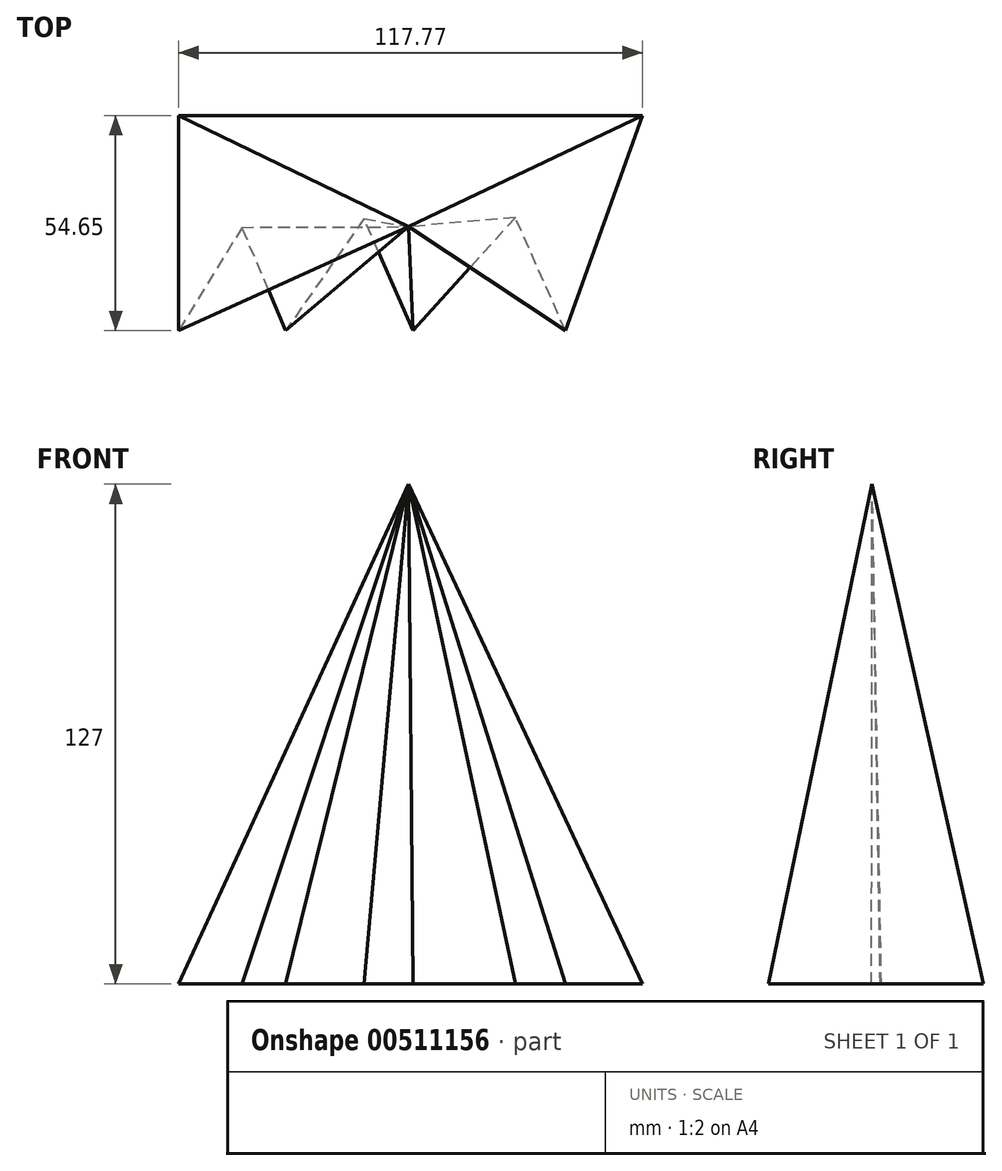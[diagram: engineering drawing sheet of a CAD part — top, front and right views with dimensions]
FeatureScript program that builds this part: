
annotation { "Feature Type Name" : "Feature", "Feature Type Description" : "" }
export const myFeature = defineFeature(function(context is Context, id is Id, definition is map)
    precondition{}
    {
        {
            var Q0;
            Q0=qCreatedBy(makeId("Top.planeOp"),FACE);
            var sketch = newSketch(context, id + "F0", { "sketchPlane" : qUnion([Q0])});
            skLineSegment(sketch, "E0", {"start": v(-59.46, 54.65) * mm, "end": v(58.3, 54.65) * mm});
            skLineSegment(sketch, "E1", {"start": v(58.3, 54.65) * mm, "end": v(38.77, 0) * mm});
            skLineSegment(sketch, "E2", {"start": v(38.77, 0) * mm, "end": v(26.04, 28.72) * mm});
            skLineSegment(sketch, "E3", {"start": v(26.04, 28.72) * mm, "end": v(0, 0) * mm});
            skLineSegment(sketch, "E4", {"start": v(0, 0) * mm, "end": v(-12.43, 28.44) * mm});
            skLineSegment(sketch, "E5", {"start": v(-12.43, 28.44) * mm, "end": v(-32.35, 0) * mm});
            skLineSegment(sketch, "E6", {"start": v(-32.35, 0) * mm, "end": v(-43.42, 26.23) * mm});
            skLineSegment(sketch, "E7", {"start": v(-43.42, 26.23) * mm, "end": v(-59.47, 0) * mm});
            skLineSegment(sketch, "E8", {"start": v(-59.47, 0) * mm, "end": v(-59.46, 54.65) * mm});
            skLineSegment(sketch, "E9", {"start": v(103.24, 44.22) * mm, "end": v(103.24, 40.62) * mm});
            skSolve(sketch);
        }
        {
            var Q0;
            Q0=makeQuery(id+"F0.imprint","IMPRINT",FACE,{"disambiguationData":[TD([[makeQuery(id+"F0.imprint","IMPRINT",EDGE,{"derivedFrom":sQuery(id+"F0.wireOp",EDGE,"E0")}),-1.0]])]});
            cPlane(context, id + "F1", {"entities" : qUnion([Q0]), "cplaneType" : CPlaneType.OFFSET, "offset" : 127 * mm, "width" : 152.4 * mm, "height" : 152.4 * mm});
        }
        {
            var Q0;
            Q0=qCreatedBy(id+"F1.planeOp",FACE);
            var sketch = newSketch(context, id + "F2", { "sketchPlane" : qUnion([Q0])});
            skPoint(sketch, "E10", {"position": v(-1.05, 26.38) * mm});
            skSolve(sketch);
        }
        {
            var Q0;
            Q0=makeQuery(id+"F0.imprint","IMPRINT",FACE,{"disambiguationData":[TD([[makeQuery(id+"F0.imprint","IMPRINT",EDGE,{"derivedFrom":sQuery(id+"F0.wireOp",EDGE,"E0")}),-1.0]])]});
            var Q1;
            Q1=sQuery(id+"F2.wireOp",VERTEX,"E10");
            loft(context, id + "F3", {"sheetProfilesArray" : [{ "sheetProfileEntities" : qUnion([Q0]) }, { "sheetProfileEntities" : qUnion([Q1]) }]});
        }
    });
